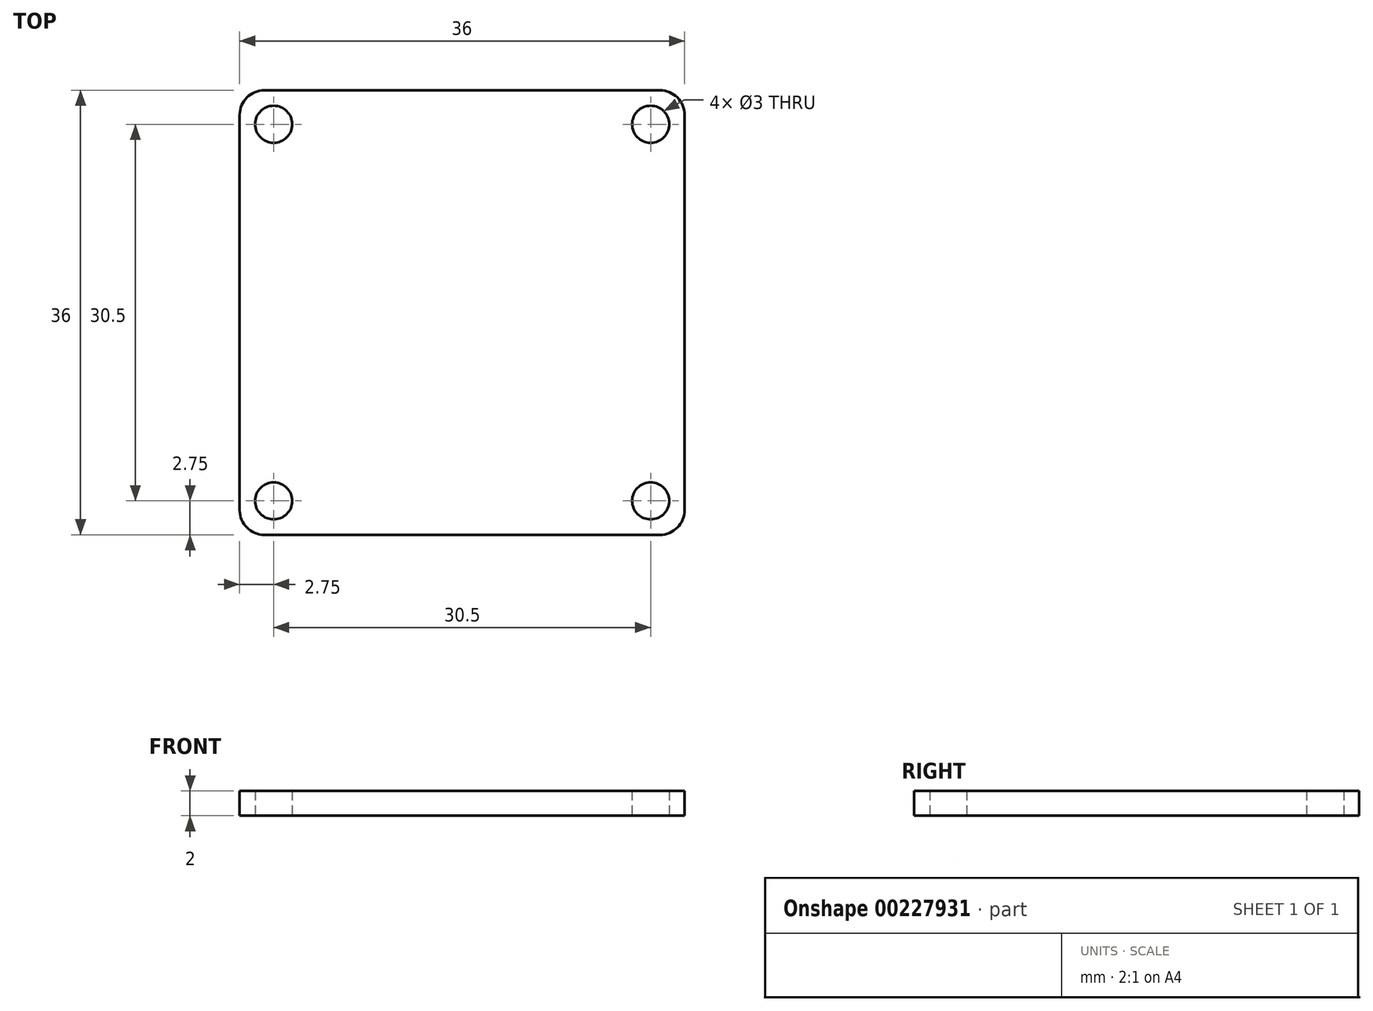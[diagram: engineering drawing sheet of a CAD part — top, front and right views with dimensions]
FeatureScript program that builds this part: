
annotation { "Feature Type Name" : "Feature", "Feature Type Description" : "" }
export const myFeature = defineFeature(function(context is Context, id is Id, definition is map)
    precondition{}
    {
        {
            var Q0;
            Q0=qCreatedBy(makeId("Top.planeOp"),FACE);
            var sketch = newSketch(context, id + "F0", { "sketchPlane" : qUnion([Q0])});
            skLineSegment(sketch, "E0.bottom", {"start": v(-16, 18) * mm, "end": v(16, 18) * mm});
            skLineSegment(sketch, "E0.top", {"start": v(-16, -18) * mm, "end": v(16, -18) * mm});
            skLineSegment(sketch, "E0.left", {"start": v(-18, 16) * mm, "end": v(-18, -16) * mm});
            skLineSegment(sketch, "E0.right", {"start": v(18, 16) * mm, "end": v(18, -16) * mm});
            skLineSegment(sketch, "E1", {"start": v(-18, 18) * mm, "end": v(18, -18) * mm, "construction": true});
            skLineSegment(sketch, "E2", {"start": v(18, 18) * mm, "end": v(-18, -18) * mm, "construction": true});
            skCircle(sketch, "E3", {"center": v(-15.25, 15.25) * mm, "radius": 1.5 * mm});
            skCircle(sketch, "E4.1.0", {"center": v(-15.25, -15.25) * mm, "radius": 1.5 * mm});
            skCircle(sketch, "E4.2.0", {"center": v(15.25, -15.25) * mm, "radius": 1.5 * mm});
            skPoint(sketch, "E4.center", {"position": v(0, 0) * mm});
            skCircle(sketch, "E5.1.3.0", {"center": v(15.25, 15.25) * mm, "radius": 1.5 * mm});
            skPoint(sketch, "E6.visualSharp", {"position": v(-18, 18) * mm});
            skArc(sketch, "E6.filletArc", {"start": v(-16, 18) * mm, "mid": v(-17.41, 17.41) * mm, "end": v(-18, 16) * mm});
            skPoint(sketch, "E7.visualSharp", {"position": v(18, 18) * mm});
            skArc(sketch, "E7.filletArc", {"start": v(18, 16) * mm, "mid": v(17.41, 17.41) * mm, "end": v(16, 18) * mm});
            skPoint(sketch, "E8.visualSharp", {"position": v(18, -18) * mm});
            skArc(sketch, "E8.filletArc", {"start": v(16, -18) * mm, "mid": v(17.41, -17.41) * mm, "end": v(18, -16) * mm});
            skPoint(sketch, "E9.visualSharp", {"position": v(-18, -18) * mm});
            skArc(sketch, "E9.filletArc", {"start": v(-18, -16) * mm, "mid": v(-17.41, -17.41) * mm, "end": v(-16, -18) * mm});
            skSolve(sketch);
        }
        {
            var Q0;
            Q0=makeQuery(id+"F0.imprint","IMPRINT",FACE,{"disambiguationData":[TD([[makeQuery(id+"F0.imprint","IMPRINT",EDGE,{"derivedFrom":sQuery(id+"F0.wireOp",EDGE,"E0.bottom")}),-1.0]])]});
            extrude(context, id + "F1", {"entities" : qUnion([Q0]), "depth" : 2 * mm});
        }
    });
